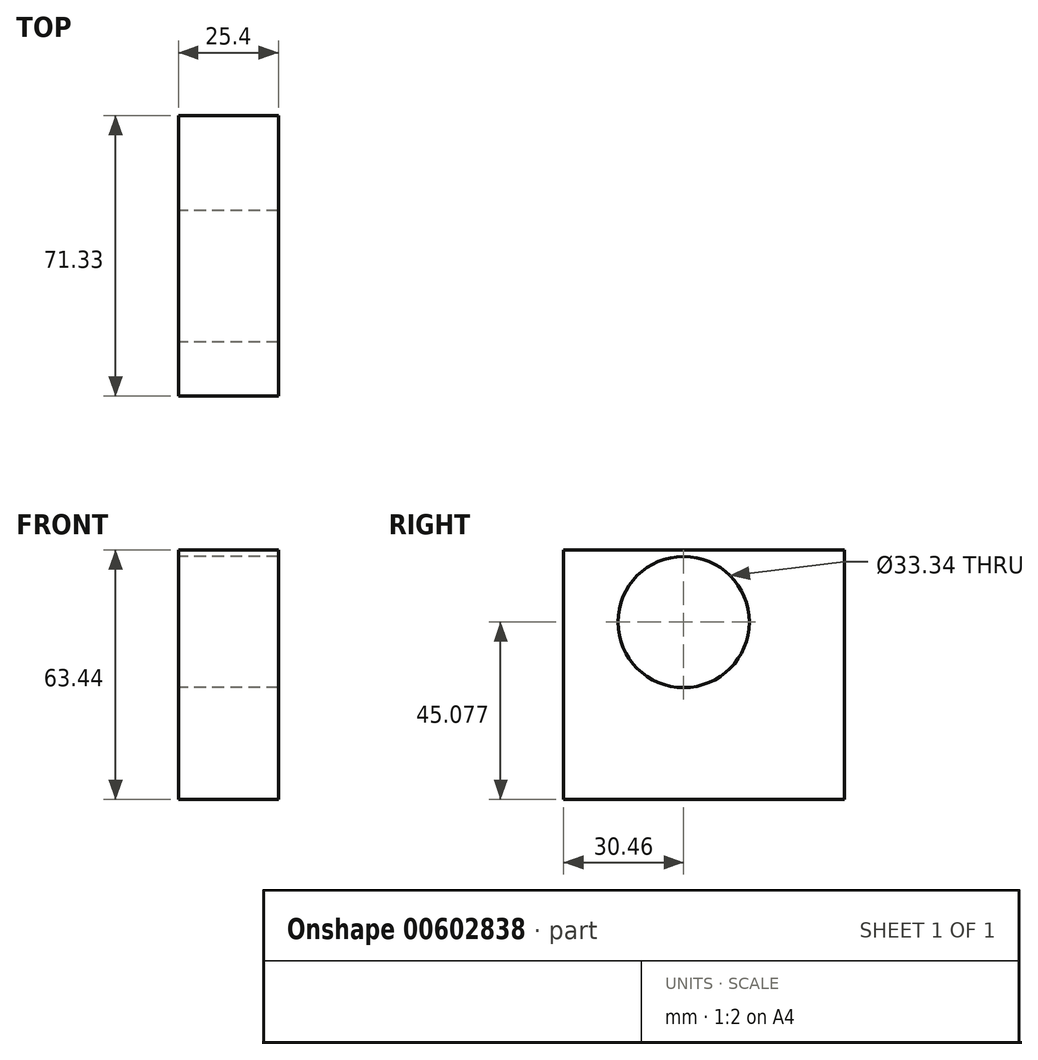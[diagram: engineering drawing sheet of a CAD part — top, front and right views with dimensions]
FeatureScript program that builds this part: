
annotation { "Feature Type Name" : "Feature", "Feature Type Description" : "" }
export const myFeature = defineFeature(function(context is Context, id is Id, definition is map)
    precondition{}
    {
        {
            var Q0;
            Q0=qCreatedBy(makeId("Right.planeOp"),FACE);
            var sketch = newSketch(context, id + "F0", { "sketchPlane" : qUnion([Q0])});
            skLineSegment(sketch, "E0.bottom", {"start": v(-30.46, -24.93) * mm, "end": v(40.87, -24.93) * mm});
            skLineSegment(sketch, "E0.top", {"start": v(-30.46, 38.5) * mm, "end": v(40.87, 38.5) * mm});
            skLineSegment(sketch, "E0.left", {"start": v(-30.46, -24.93) * mm, "end": v(-30.46, 38.5) * mm});
            skLineSegment(sketch, "E0.right", {"start": v(40.87, -24.93) * mm, "end": v(40.87, 38.5) * mm});
            skSolve(sketch);
        }
        {
            var Q0;
            Q0=makeQuery(id+"F0.imprint","IMPRINT",FACE,{"disambiguationData":[TD([[makeQuery(id+"F0.imprint","IMPRINT",EDGE,{"derivedFrom":sQuery(id+"F0.wireOp",EDGE,"E0.bottom")}),1.0]])]});
            extrude(context, id + "F1", {"entities" : qUnion([Q0]), "depth" : 25.4 * mm, "offsetDistance" : 25.4 * mm});
        }
        {
            var Q0;
            Q0=makeQuery(id+"F1.opExtrude","CAP_FACE",FACE,{"disambiguationData":[OSD([sQuery(id+"F0.wireOp",EDGE,"E0.bottom"),sQuery(id+"F0.wireOp",EDGE,"E0.top"),sQuery(id+"F0.wireOp",EDGE,"E0.left"),sQuery(id+"F0.wireOp",EDGE,"E0.right")])],"isStart":true});
            var sketch = newSketch(context, id + "F2", { "sketchPlane" : qUnion([Q0])});
            skCircle(sketch, "E1", {"center": v(0, 20.15) * mm, "radius": 16.67 * mm});
            skSolve(sketch);
        }
        {
            var Q0;
            Q0=makeQuery(id+"F2.imprint","IMPRINT",FACE,{"disambiguationData":[TD([[makeQuery(id+"F2.imprint","IMPRINT",EDGE,{"derivedFrom":sQuery(id+"F2.wireOp",EDGE,"E1")}),1.0]])]});
            extrude(context, id + "F3", {"entities" : qUnion([Q0]), "operationType" : NewBodyOperationType.REMOVE, "oppositeDirection" : true, "depth" : 25.4 * mm, "offsetDistance" : 25.4 * mm});
        }
    });
